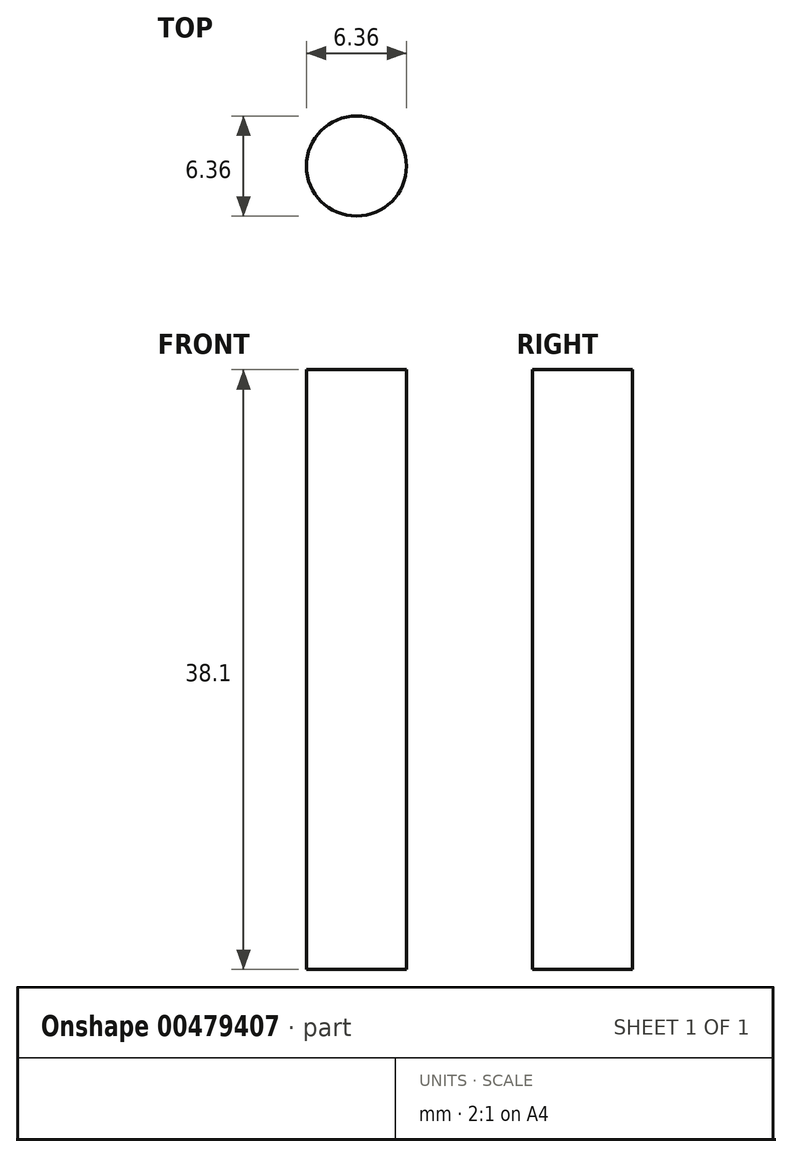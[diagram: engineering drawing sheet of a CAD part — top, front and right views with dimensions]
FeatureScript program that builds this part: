
annotation { "Feature Type Name" : "Feature", "Feature Type Description" : "" }
export const myFeature = defineFeature(function(context is Context, id is Id, definition is map)
    precondition{}
    {
        {
            var Q0;
            Q0=qCreatedBy(makeId("Top.planeOp"),FACE);
            var sketch = newSketch(context, id + "F0", { "sketchPlane" : qUnion([Q0])});
            skCircle(sketch, "E0", {"center": v(0, 0) * mm, "radius": 3.18 * mm});
            skSolve(sketch);
        }
        {
            var Q0;
            Q0 = qSketchRegion(id + "F0", true);
            extrude(context, id + "F1", {"entities" : qUnion([Q0]), "depth" : 38.1 * mm, "offsetDistance" : 25.4 * mm});
        }
    });
